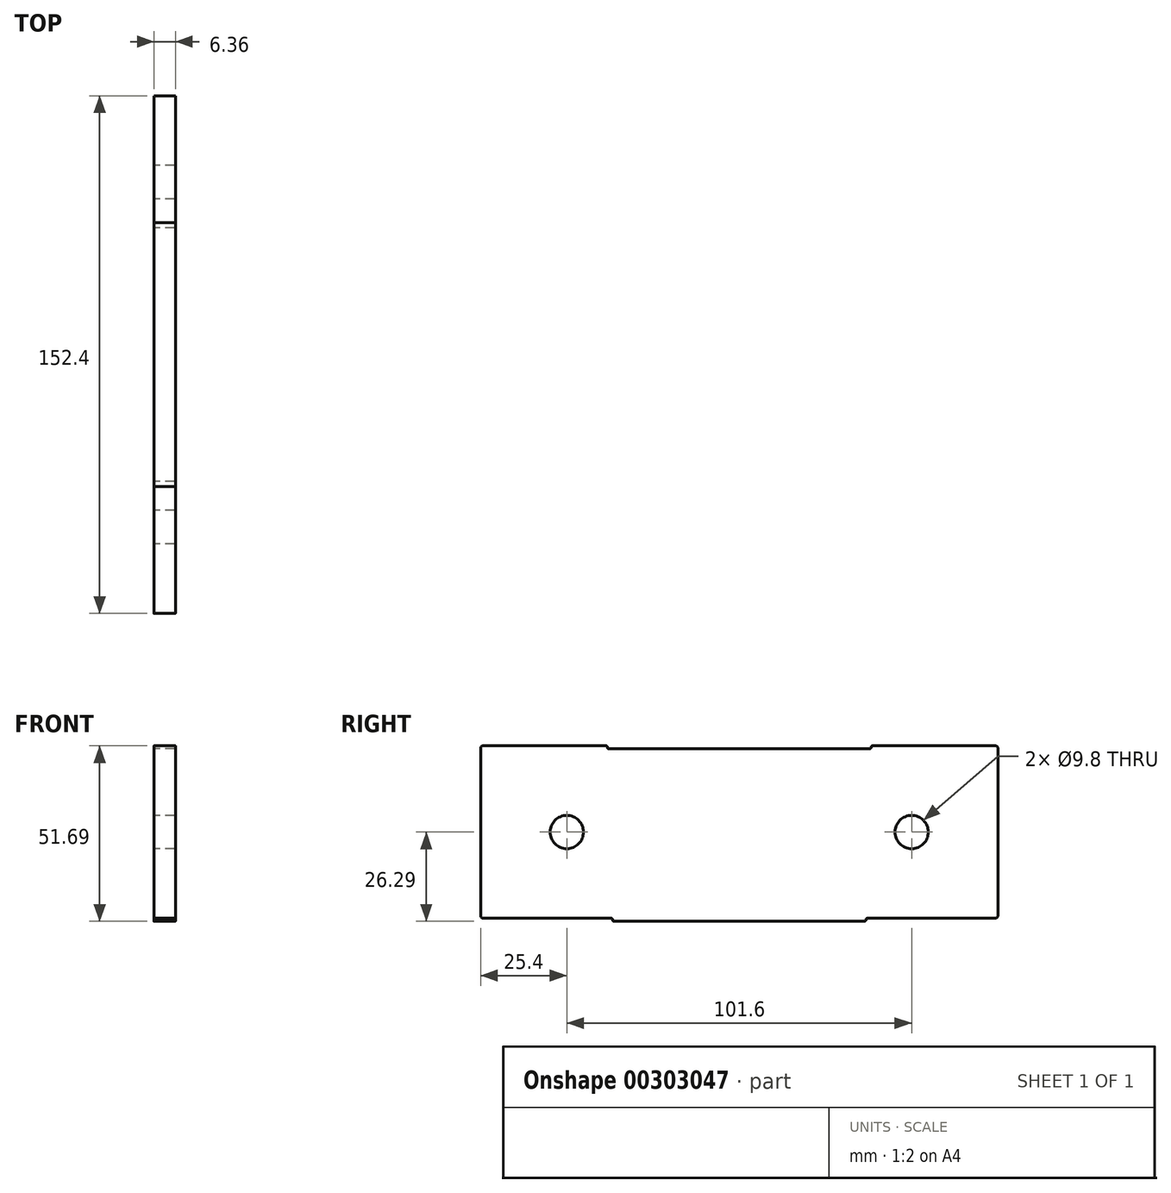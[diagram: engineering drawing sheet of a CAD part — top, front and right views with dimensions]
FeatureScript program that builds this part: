
annotation { "Feature Type Name" : "Feature", "Feature Type Description" : "" }
export const myFeature = defineFeature(function(context is Context, id is Id, definition is map)
    precondition{}
    {
        {
            var Q0;
            Q0=qCreatedBy(makeId("Right.planeOp"),FACE);
            var sketch = newSketch(context, id + "F0", { "sketchPlane" : qUnion([Q0])});
            skLineSegment(sketch, "E0", {"start": v(-75.44, 25.4) * mm, "end": v(-39.27, 25.4) * mm});
            skLineSegment(sketch, "E1", {"start": v(-38.86, 25) * mm, "end": v(-38.86, 24.92) * mm});
            skLineSegment(sketch, "E2", {"start": v(-38.46, 24.51) * mm, "end": v(0, 24.51) * mm});
            skLineSegment(sketch, "E3", {"start": v(0, -26.29) * mm, "end": v(-36.93, -26.29) * mm});
            skLineSegment(sketch, "E4", {"start": v(-37.34, -25.88) * mm, "end": v(-37.34, -25.8) * mm});
            skLineSegment(sketch, "E5", {"start": v(-37.74, -25.4) * mm, "end": v(-75.44, -25.4) * mm});
            skLineSegment(sketch, "E6", {"start": v(-76.2, -24.64) * mm, "end": v(-76.2, 24.64) * mm});
            skArc(sketch, "E7", {"start": v(-38.86, 25) * mm, "mid": v(-38.98, 25.28) * mm, "end": v(-39.27, 25.4) * mm});
            skArc(sketch, "E8", {"start": v(-38.86, 24.92) * mm, "mid": v(-38.74, 24.63) * mm, "end": v(-38.46, 24.51) * mm});
            skArc(sketch, "E9", {"start": v(-75.44, 25.4) * mm, "mid": v(-75.98, 25.18) * mm, "end": v(-76.2, 24.64) * mm});
            skArc(sketch, "E10", {"start": v(-76.2, -24.64) * mm, "mid": v(-75.98, -25.18) * mm, "end": v(-75.44, -25.4) * mm});
            skArc(sketch, "E11", {"start": v(-37.34, -25.8) * mm, "mid": v(-37.46, -25.52) * mm, "end": v(-37.74, -25.4) * mm});
            skArc(sketch, "E12", {"start": v(-37.34, -25.88) * mm, "mid": v(-37.22, -26.17) * mm, "end": v(-36.93, -26.29) * mm});
            skArc(sketch, "E13.MirrorCS", {"start": v(37.34, -25.8) * mm, "mid": v(37.46, -25.52) * mm, "end": v(37.74, -25.4) * mm});
            skArc(sketch, "E14.MirrorCS", {"start": v(75.44, 25.4) * mm, "mid": v(75.98, 25.18) * mm, "end": v(76.2, 24.64) * mm});
            skLineSegment(sketch, "E15.MirrorCS", {"start": v(38.86, 25) * mm, "end": v(38.86, 24.92) * mm});
            skLineSegment(sketch, "E16.MirrorCS", {"start": v(37.34, -25.88) * mm, "end": v(37.34, -25.8) * mm});
            skArc(sketch, "E17.MirrorCS", {"start": v(37.34, -25.88) * mm, "mid": v(37.22, -26.17) * mm, "end": v(36.93, -26.29) * mm});
            skArc(sketch, "E18.MirrorCS", {"start": v(38.86, 25) * mm, "mid": v(38.98, 25.28) * mm, "end": v(39.27, 25.4) * mm});
            skArc(sketch, "E19.MirrorCS", {"start": v(38.86, 24.92) * mm, "mid": v(38.74, 24.63) * mm, "end": v(38.46, 24.51) * mm});
            skLineSegment(sketch, "E20.MirrorCS", {"start": v(75.44, 25.4) * mm, "end": v(39.27, 25.4) * mm});
            skLineSegment(sketch, "E21.MirrorCS", {"start": v(38.46, 24.51) * mm, "end": v(0, 24.51) * mm});
            skLineSegment(sketch, "E22.MirrorCS", {"start": v(0, -26.29) * mm, "end": v(36.93, -26.29) * mm});
            skArc(sketch, "E23.MirrorCS", {"start": v(76.2, -24.64) * mm, "mid": v(75.98, -25.18) * mm, "end": v(75.44, -25.4) * mm});
            skLineSegment(sketch, "E24.MirrorCS", {"start": v(37.74, -25.4) * mm, "end": v(75.44, -25.4) * mm});
            skLineSegment(sketch, "E25.MirrorCS", {"start": v(76.2, -24.64) * mm, "end": v(76.2, 24.64) * mm});
            skCircle(sketch, "E26", {"center": v(-50.8, 0) * mm, "radius": 4.9 * mm});
            skCircle(sketch, "E27.MirrorC", {"center": v(50.8, 0) * mm, "radius": 4.9 * mm});
            skSolve(sketch);
        }
        {
            var Q0;
            Q0=makeQuery(id+"F0.imprint","IMPRINT",FACE,{"disambiguationData":[TD([[makeQuery(id+"F0.imprint","IMPRINT",EDGE,{"derivedFrom":sQuery(id+"F0.wireOp",EDGE,"E0")}),-1.0]])]});
            extrude(context, id + "F1", {"entities" : qUnion([Q0]), "depth" : 6.35 * mm, "symmetric" : true});
        }
    });
